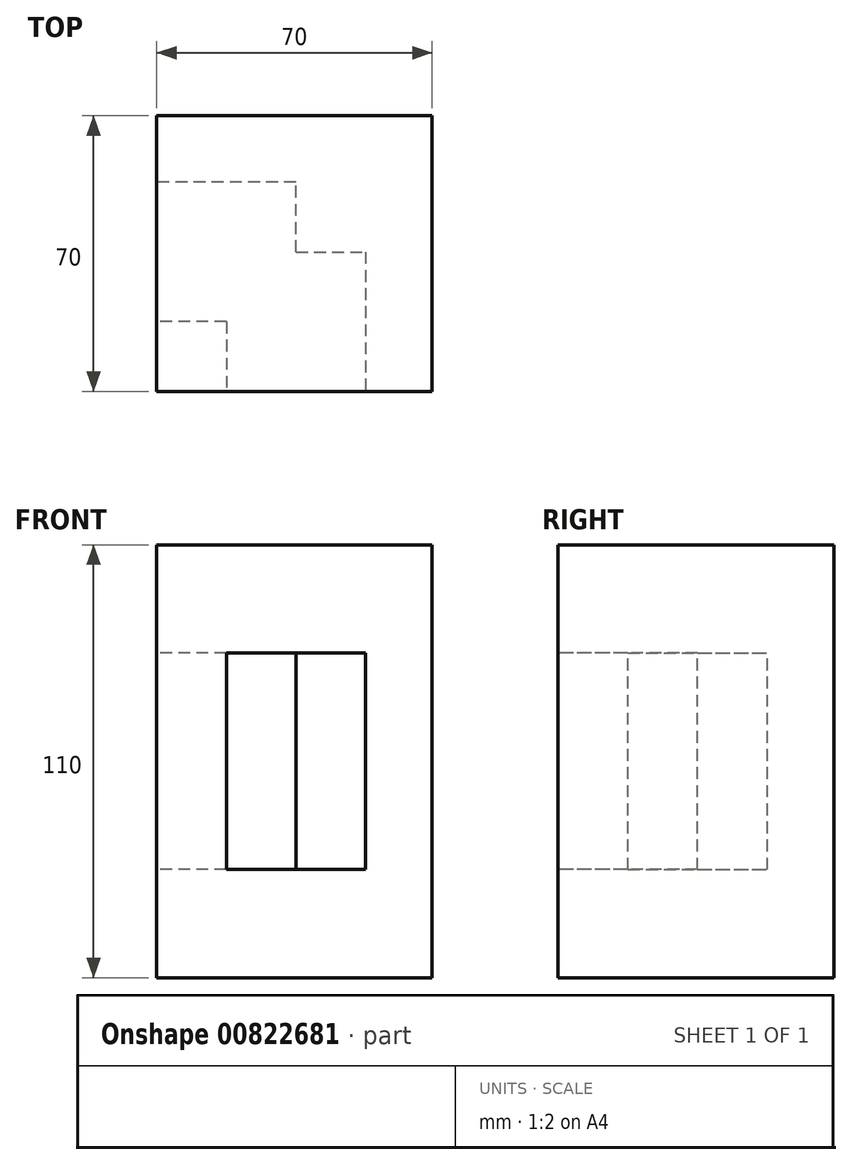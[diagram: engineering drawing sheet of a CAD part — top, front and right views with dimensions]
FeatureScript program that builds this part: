
annotation { "Feature Type Name" : "Feature", "Feature Type Description" : "" }
export const myFeature = defineFeature(function(context is Context, id is Id, definition is map)
    precondition{}
    {
        {
            var Q0;
            Q0=qCreatedBy(makeId("Top.planeOp"),FACE);
            var sketch = newSketch(context, id + "F0", { "sketchPlane" : qUnion([Q0])});
            skLineSegment(sketch, "E0.bottom", {"start": v(0, -17.7) * mm, "end": v(-35.4, -17.7) * mm});
            skLineSegment(sketch, "E0.top", {"start": v(0, 17.7) * mm, "end": v(-35.4, 17.7) * mm});
            skLineSegment(sketch, "E0.left", {"start": v(0, -17.7) * mm, "end": v(0, 17.7) * mm});
            skLineSegment(sketch, "E0.right", {"start": v(-35.4, -17.7) * mm, "end": v(-35.4, 17.7) * mm});
            skLineSegment(sketch, "E1.bottom", {"start": v(-17.7, 0) * mm, "end": v(17.7, 0) * mm});
            skLineSegment(sketch, "E1.top", {"start": v(-17.7, -35.4) * mm, "end": v(17.7, -35.4) * mm});
            skLineSegment(sketch, "E1.left", {"start": v(-17.7, 0) * mm, "end": v(-17.7, -35.4) * mm});
            skLineSegment(sketch, "E1.right", {"start": v(17.7, 0) * mm, "end": v(17.7, -35.4) * mm});
            skLineSegment(sketch, "E2.bottom", {"start": v(-35.4, 34.6) * mm, "end": v(34.6, 34.6) * mm});
            skLineSegment(sketch, "E2.top", {"start": v(-35.4, -35.4) * mm, "end": v(34.6, -35.4) * mm});
            skLineSegment(sketch, "E2.left", {"start": v(-35.4, 34.6) * mm, "end": v(-35.4, -35.4) * mm});
            skLineSegment(sketch, "E2.right", {"start": v(34.6, 34.6) * mm, "end": v(34.6, -35.4) * mm});
            skSolve(sketch);
        }
        {
            var Q0;
            {var subQ2=sQuery(id+"F0.wireOp",EDGE,"E0.top");Q0=makeQuery(id+"F0.imprint","IMPRINT",FACE,{"disambiguationData":[TD([[makeQuery(id+"F0.imprint","IMPRINT",EDGE,{"derivedFrom":subQ2}),-1.0]])]});}
            var Q1;
            {var subQ1=sQuery(id+"F0.wireOp",EDGE,"E0.top");Q1=makeQuery(id+"F0.imprint","IMPRINT",FACE,{"disambiguationData":[TD([[makeQuery(id+"F0.imprint","IMPRINT",EDGE,{"derivedFrom":subQ1}),1.0]])]});}
            var Q2;
            {var subQ0=sQuery(id+"F0.wireOp",EDGE,"E1.left");var subQ1=sQuery(id+"F0.wireOp",EDGE,"E0.bottom");var subQ2=makeQuery(id+"F0.imprint","INTERSECT",VERTEX,{"derivedFrom":[subQ1,subQ0]});Q2=makeQuery(id+"F0.imprint","IMPRINT",FACE,{"disambiguationData":[TD([[makeQuery(id+"F0.imprint","IMPRINT",EDGE,{"disambiguationData":[TD([[subQ2,1.0]])],"derivedFrom":subQ1}),-1.0]])]});}
            var Q3;
            {var subQ0=sQuery(id+"F0.wireOp",EDGE,"E1.top");Q3=makeQuery(id+"F0.imprint","IMPRINT",FACE,{"disambiguationData":[TD([[makeQuery(id+"F0.imprint","IMPRINT",EDGE,{"derivedFrom":subQ0}),1.0]])]});}
            var Q4;
            {var subQ0=sQuery(id+"F0.wireOp",EDGE,"E1.left");var subQ1=sQuery(id+"F0.wireOp",EDGE,"E0.bottom");var subQ2=makeQuery(id+"F0.imprint","INTERSECT",VERTEX,{"derivedFrom":[subQ1,subQ0]});Q4=makeQuery(id+"F0.imprint","IMPRINT",FACE,{"disambiguationData":[TD([[makeQuery(id+"F0.imprint","IMPRINT",EDGE,{"disambiguationData":[TD([[subQ2,-1.0]])],"derivedFrom":subQ1}),1.0]])]});}
            extrude(context, id + "F1", {"entities" : qUnion([Q0, Q1, Q2, Q3, Q4]), "endBound" : BoundingType.SYMMETRIC, "depth" : 110 * mm, "offsetDistance" : 25 * mm});
        }
        {
            var Q0;
            {var subQ1=sQuery(id+"F0.wireOp",EDGE,"E0.top");Q0=makeQuery(id+"F0.imprint","IMPRINT",FACE,{"disambiguationData":[TD([[makeQuery(id+"F0.imprint","IMPRINT",EDGE,{"derivedFrom":subQ1}),1.0]])]});}
            var Q1;
            {var subQ0=sQuery(id+"F0.wireOp",EDGE,"E1.left");var subQ1=sQuery(id+"F0.wireOp",EDGE,"E0.bottom");var subQ2=makeQuery(id+"F0.imprint","INTERSECT",VERTEX,{"derivedFrom":[subQ1,subQ0]});Q1=makeQuery(id+"F0.imprint","IMPRINT",FACE,{"disambiguationData":[TD([[makeQuery(id+"F0.imprint","IMPRINT",EDGE,{"disambiguationData":[TD([[subQ2,1.0]])],"derivedFrom":subQ1}),-1.0]])]});}
            var Q2;
            {var subQ0=sQuery(id+"F0.wireOp",EDGE,"E1.top");Q2=makeQuery(id+"F0.imprint","IMPRINT",FACE,{"disambiguationData":[TD([[makeQuery(id+"F0.imprint","IMPRINT",EDGE,{"derivedFrom":subQ0}),1.0]])]});}
            extrude(context, id + "F2", {"entities" : qUnion([Q0, Q1, Q2]), "operationType" : NewBodyOperationType.REMOVE, "endBound" : BoundingType.SYMMETRIC, "oppositeDirection" : true, "depth" : 55 * mm, "offsetDistance" : 25 * mm});
        }
    });
